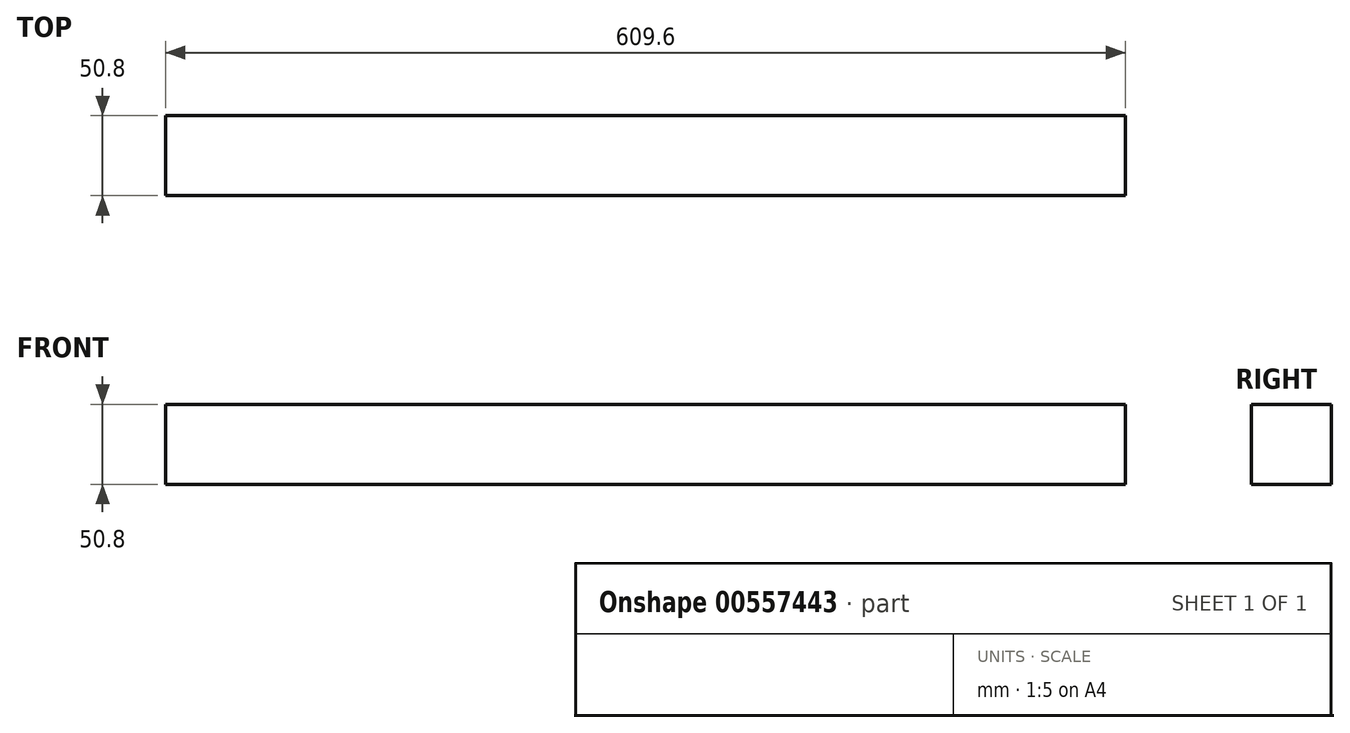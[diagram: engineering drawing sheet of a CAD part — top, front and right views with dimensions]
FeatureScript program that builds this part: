
annotation { "Feature Type Name" : "Feature", "Feature Type Description" : "" }
export const myFeature = defineFeature(function(context is Context, id is Id, definition is map)
    precondition{}
    {
        {
            var Q0;
            Q0=qCreatedBy(makeId("Front.planeOp"),FACE);
            var sketch = newSketch(context, id + "F0", { "sketchPlane" : qUnion([Q0])});
            skLineSegment(sketch, "E0.bottom", {"start": v(-609.6, 0) * mm, "end": v(0, 0) * mm});
            skLineSegment(sketch, "E0.top", {"start": v(-609.6, 50.8) * mm, "end": v(0, 50.8) * mm});
            skLineSegment(sketch, "E0.left", {"start": v(-609.6, 0) * mm, "end": v(-609.6, 50.8) * mm});
            skLineSegment(sketch, "E0.right", {"start": v(0, 0) * mm, "end": v(0, 50.8) * mm});
            skSolve(sketch);
        }
        {
            var Q0;
            Q0=makeQuery(id+"F0.imprint","IMPRINT",FACE,{"disambiguationData":[TD([[makeQuery(id+"F0.imprint","IMPRINT",EDGE,{"derivedFrom":sQuery(id+"F0.wireOp",EDGE,"E0.bottom")}),1.0]])]});
            extrude(context, id + "F1", {"entities" : qUnion([Q0]), "depth" : 50.8 * mm, "offsetDistance" : 25.4 * mm});
        }
    });
